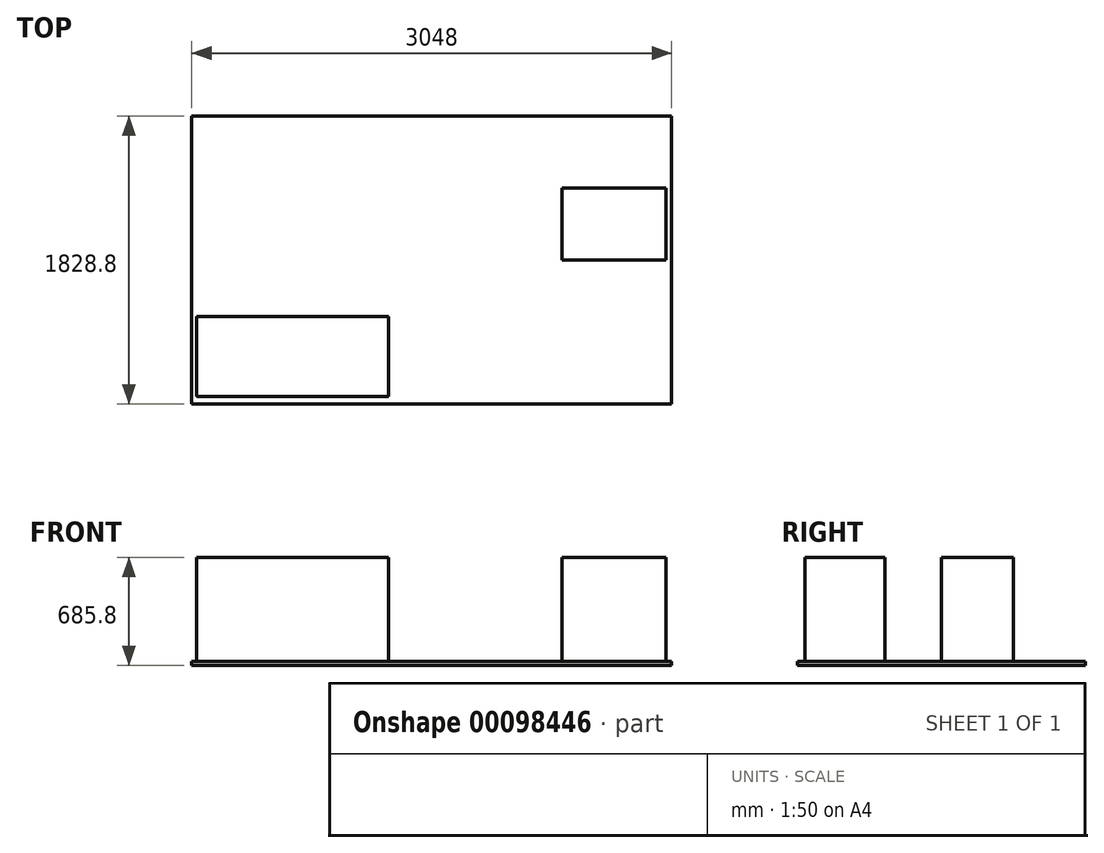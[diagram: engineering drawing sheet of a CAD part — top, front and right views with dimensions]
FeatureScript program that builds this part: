
annotation { "Feature Type Name" : "Feature", "Feature Type Description" : "" }
export const myFeature = defineFeature(function(context is Context, id is Id, definition is map)
    precondition{}
    {
        {
            var Q0;
            Q0=qCreatedBy(makeId("Top.planeOp"),FACE);
            var sketch = newSketch(context, id + "F0", { "sketchPlane" : qUnion([Q0])});
            skLineSegment(sketch, "E0.bottom", {"start": v(-1524, 914.4) * mm, "end": v(1524, 914.4) * mm});
            skLineSegment(sketch, "E0.top", {"start": v(-1524, -914.4) * mm, "end": v(1524, -914.4) * mm});
            skLineSegment(sketch, "E0.left", {"start": v(-1524, 914.4) * mm, "end": v(-1524, -914.4) * mm});
            skLineSegment(sketch, "E0.right", {"start": v(1524, 914.4) * mm, "end": v(1524, -914.4) * mm});
            skPoint(sketch, "E0.middle", {"position": v(0, 0) * mm});
            skSolve(sketch);
        }
        {
            var Q0;
            Q0=qCreatedBy(makeId("Top.planeOp"),FACE);
            var sketch = newSketch(context, id + "F1", { "sketchPlane" : qUnion([Q0])});
            skLineSegment(sketch, "E1.bottom", {"start": v(-1493.12, -867.4) * mm, "end": v(-273.92, -867.4) * mm});
            skLineSegment(sketch, "E1.top", {"start": v(-1493.12, -359.4) * mm, "end": v(-273.92, -359.4) * mm});
            skLineSegment(sketch, "E1.left", {"start": v(-1493.12, -867.4) * mm, "end": v(-1493.12, -359.4) * mm});
            skLineSegment(sketch, "E1.right", {"start": v(-273.92, -867.4) * mm, "end": v(-273.92, -359.4) * mm});
            skLineSegment(sketch, "E2.bottom", {"start": v(828.37, 457.2) * mm, "end": v(1488.77, 457.2) * mm});
            skLineSegment(sketch, "E2.top", {"start": v(828.37, 0) * mm, "end": v(1488.77, 0) * mm});
            skLineSegment(sketch, "E2.left", {"start": v(828.37, 457.2) * mm, "end": v(828.37, 0) * mm});
            skLineSegment(sketch, "E2.right", {"start": v(1488.77, 457.2) * mm, "end": v(1488.77, 0) * mm});
            skSolve(sketch);
        }
        {
            var Q0;
            Q0=makeQuery(id+"F0.imprint","IMPRINT",FACE,{"disambiguationData":[TD([[makeQuery(id+"F0.imprint","IMPRINT",EDGE,{"derivedFrom":sQuery(id+"F0.wireOp",EDGE,"E0.bottom")}),-1.0]])]});
            extrude(context, id + "F2", {"entities" : qUnion([Q0]), "oppositeDirection" : true, "depth" : 25.4 * mm});
        }
        {
            var Q0;
            Q0=makeQuery(id+"F1.imprint","IMPRINT",FACE,{"disambiguationData":[TD([[makeQuery(id+"F1.imprint","IMPRINT",EDGE,{"derivedFrom":sQuery(id+"F1.wireOp",EDGE,"E1.bottom")}),1.0]])]});
            var Q1;
            Q1=makeQuery(id+"F1.imprint","IMPRINT",FACE,{"disambiguationData":[TD([[makeQuery(id+"F1.imprint","IMPRINT",EDGE,{"derivedFrom":sQuery(id+"F1.wireOp",EDGE,"E2.bottom")}),-1.0]])]});
            extrude(context, id + "F3", {"entities" : qUnion([Q0, Q1]), "depth" : 660.4 * mm});
        }
    });
